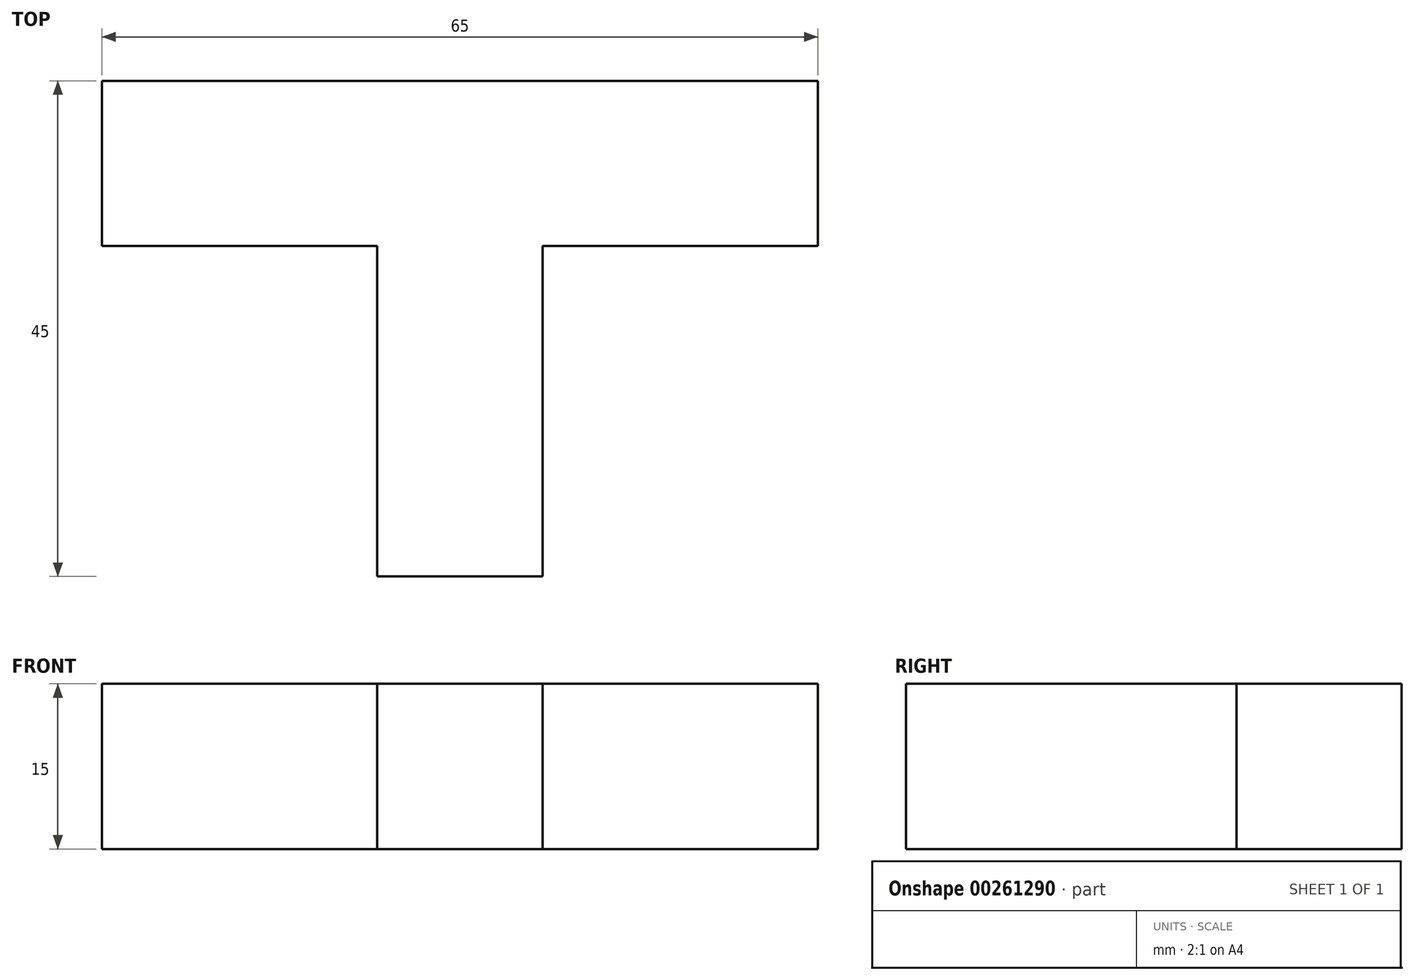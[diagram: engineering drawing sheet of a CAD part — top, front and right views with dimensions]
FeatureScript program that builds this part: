
annotation { "Feature Type Name" : "Feature", "Feature Type Description" : "" }
export const myFeature = defineFeature(function(context is Context, id is Id, definition is map)
    precondition{}
    {
        {
            var Q0;
            Q0=qCreatedBy(makeId("Top.planeOp"),FACE);
            var sketch = newSketch(context, id + "F0", { "sketchPlane" : qUnion([Q0])});
            skLineSegment(sketch, "E0.bottom", {"start": v(0, 0) * mm, "end": v(15, 0) * mm});
            skLineSegment(sketch, "E0.top", {"start": v(0, 30) * mm, "end": v(15, 30) * mm});
            skLineSegment(sketch, "E0.left", {"start": v(0, 0) * mm, "end": v(0, 30) * mm});
            skLineSegment(sketch, "E0.right", {"start": v(15, 0) * mm, "end": v(15, 30) * mm});
            skLineSegment(sketch, "E1", {"start": v(15, 30) * mm, "end": v(40, 30) * mm});
            skLineSegment(sketch, "E2", {"start": v(40, 30) * mm, "end": v(40, 45) * mm});
            skLineSegment(sketch, "E3", {"start": v(40, 45) * mm, "end": v(-25, 45) * mm});
            skLineSegment(sketch, "E4", {"start": v(-25, 45) * mm, "end": v(-25, 30) * mm});
            skLineSegment(sketch, "E5", {"start": v(-25, 30) * mm, "end": v(0, 30) * mm});
            skSolve(sketch);
        }
        {
            var Q0;
            Q0=makeQuery(id+"F0.imprint","IMPRINT",FACE,{"disambiguationData":[TD([[makeQuery(id+"F0.imprint","IMPRINT",EDGE,{"derivedFrom":sQuery(id+"F0.wireOp",EDGE,"E0.bottom")}),1.0]])]});
            var Q1;
            Q1=makeQuery(id+"F0.imprint","IMPRINT",FACE,{"disambiguationData":[TD([[makeQuery(id+"F0.imprint","IMPRINT",EDGE,{"derivedFrom":sQuery(id+"F0.wireOp",EDGE,"E0.top")}),1.0]])]});
            extrude(context, id + "F1", {"entities" : qUnion([Q0, Q1]), "depth" : 15 * mm});
        }
    });
